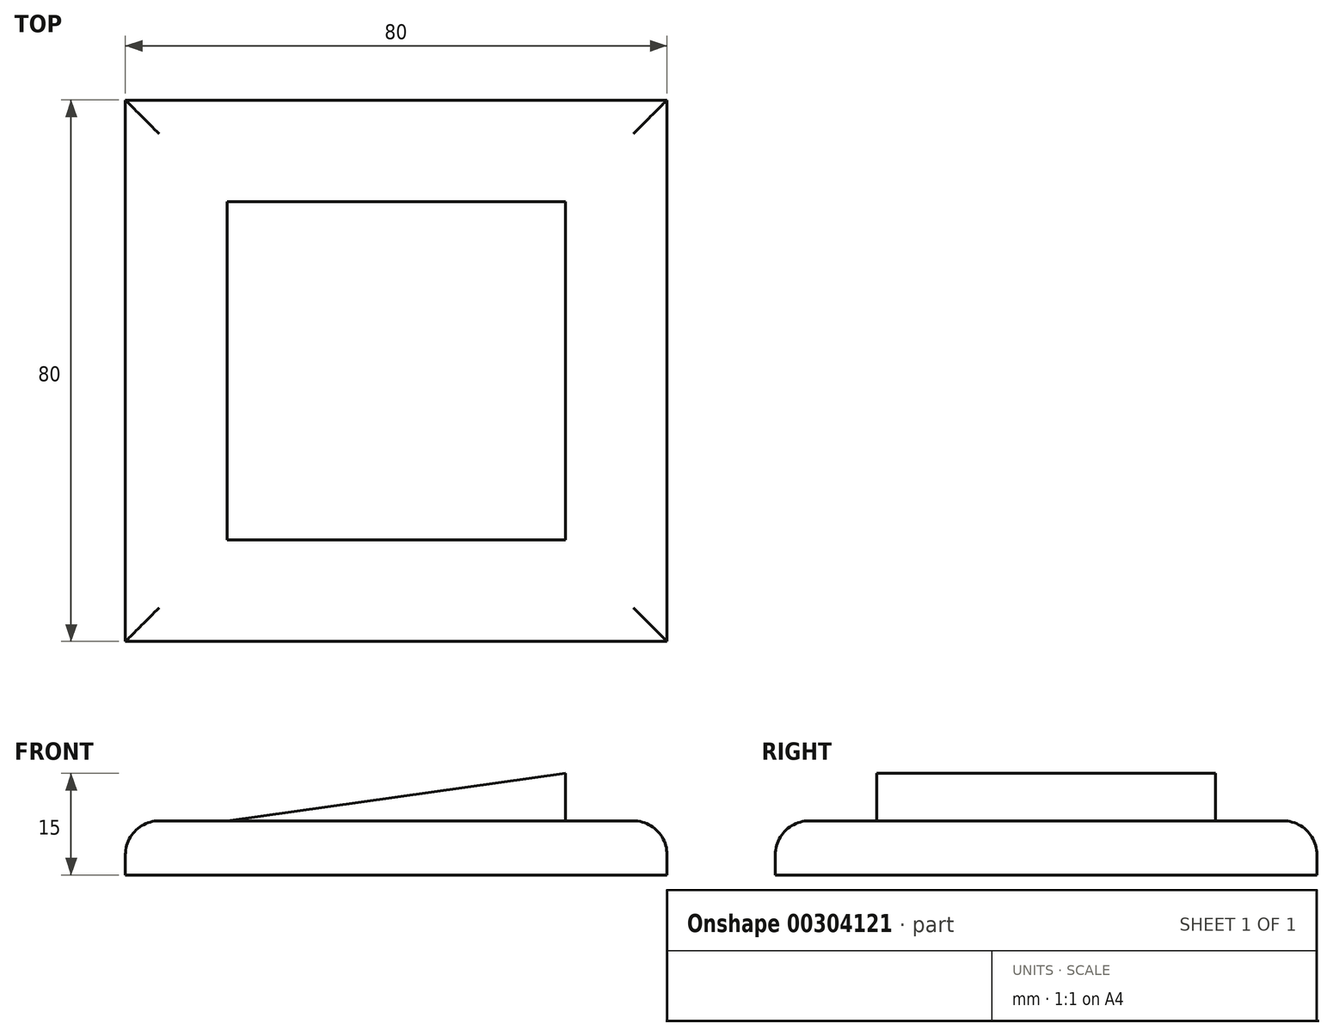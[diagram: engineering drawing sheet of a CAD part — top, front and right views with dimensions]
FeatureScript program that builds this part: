
annotation { "Feature Type Name" : "Feature", "Feature Type Description" : "" }
export const myFeature = defineFeature(function(context is Context, id is Id, definition is map)
    precondition{}
    {
        {
            var Q0;
            Q0=qCreatedBy(makeId("Top.planeOp"),FACE);
            var sketch = newSketch(context, id + "F0", { "sketchPlane" : qUnion([Q0])});
            skLineSegment(sketch, "E0.bottom", {"start": v(-66.84, 48.36) * mm, "end": v(13.16, 48.36) * mm});
            skLineSegment(sketch, "E0.top", {"start": v(-66.84, -31.64) * mm, "end": v(13.16, -31.64) * mm});
            skLineSegment(sketch, "E0.left", {"start": v(-66.84, 48.36) * mm, "end": v(-66.84, -31.64) * mm});
            skLineSegment(sketch, "E0.right", {"start": v(13.16, 48.36) * mm, "end": v(13.16, -31.64) * mm});
            skLineSegment(sketch, "E1.bottom", {"start": v(-51.84, 33.36) * mm, "end": v(-1.84, 33.36) * mm});
            skLineSegment(sketch, "E1.top", {"start": v(-51.84, -16.64) * mm, "end": v(-1.84, -16.64) * mm});
            skLineSegment(sketch, "E1.left", {"start": v(-51.84, 33.36) * mm, "end": v(-51.84, -16.64) * mm});
            skLineSegment(sketch, "E1.right", {"start": v(-1.84, 33.36) * mm, "end": v(-1.84, -16.64) * mm});
            skSolve(sketch);
        }
        {
            var Q0;
            Q0=makeQuery(id+"F0.imprint","IMPRINT",FACE,{"disambiguationData":[TD([[makeQuery(id+"F0.imprint","IMPRINT",EDGE,{"derivedFrom":sQuery(id+"F0.wireOp",EDGE,"E0.bottom")}),-1.0]])]});
            extrude(context, id + "F1", {"entities" : qUnion([Q0]), "depth" : 8 * mm, "offsetDistance" : 25 * mm});
        }
        {
            var Q0;
            Q0=makeQuery(id+"F0.imprint","IMPRINT",FACE,{"disambiguationData":[TD([[makeQuery(id+"F0.imprint","IMPRINT",EDGE,{"derivedFrom":sQuery(id+"F0.wireOp",EDGE,"E1.bottom")}),-1.0]])]});
            extrude(context, id + "F2", {"entities" : qUnion([Q0]), "operationType" : NewBodyOperationType.ADD, "depth" : 15 * mm, "offsetDistance" : 25 * mm});
        }
        {
            var Q0;
            Q0=makeQuery(id+"F2.opExtrude","SWEPT_FACE",FACE,{"disambiguationData":[OSD([sQuery(id+"F0.wireOp",EDGE,"E1.top")])]});
            var sketch = newSketch(context, id + "F3", { "sketchPlane" : qUnion([Q0])});
            skLineSegment(sketch, "E2", {"start": v(-51.84, 8) * mm, "end": v(-1.84, 15) * mm});
            skLineSegment(sketch, "E3", {"start": v(-1.84, 15) * mm, "end": v(-1.84, 8) * mm});
            skLineSegment(sketch, "E4", {"start": v(-1.84, 8) * mm, "end": v(-51.84, 8) * mm});
            skLineSegment(sketch, "E5", {"start": v(-51.84, 8) * mm, "end": v(-51.84, 15) * mm});
            skLineSegment(sketch, "E6", {"start": v(-51.84, 15) * mm, "end": v(-1.84, 15) * mm});
            skSolve(sketch);
        }
        {
            var Q0;
            Q0=makeQuery(id+"F3.imprint","IMPRINT",FACE,{"disambiguationData":[TD([[makeQuery(id+"F3.imprint","IMPRINT",EDGE,{"derivedFrom":sQuery(id+"F3.wireOp",EDGE,"E2")}),1.0]])]});
            extrude(context, id + "F4", {"entities" : qUnion([Q0]), "operationType" : NewBodyOperationType.REMOVE, "endBound" : BoundingType.UP_TO_NEXT, "oppositeDirection" : true, "depth" : 25 * mm, "offsetDistance" : 25 * mm});
        }
        {
            var Q0;
            Q0=makeQuery(id+"F1.opExtrude","CAP_EDGE",EDGE,{"disambiguationData":[OSD([sQuery(id+"F0.wireOp",EDGE,"E0.bottom")])],"isStart":false});
            var Q1;
            Q1=makeQuery(id+"F1.opExtrude","CAP_EDGE",EDGE,{"disambiguationData":[OSD([sQuery(id+"F0.wireOp",EDGE,"E0.left")])],"isStart":false});
            var Q2;
            Q2=makeQuery(id+"F1.opExtrude","CAP_EDGE",EDGE,{"disambiguationData":[OSD([sQuery(id+"F0.wireOp",EDGE,"E0.top")])],"isStart":false});
            var Q3;
            Q3=makeQuery(id+"F1.opExtrude","CAP_EDGE",EDGE,{"disambiguationData":[OSD([sQuery(id+"F0.wireOp",EDGE,"E0.right")])],"isStart":false});
            fillet(context, id + "F5", {"entities" : qUnion([Q0, Q1, Q2, Q3]), "radius" : 5 * mm, "tangentPropagation" : true, "allowEdgeOverflow" : false});
        }
    });
